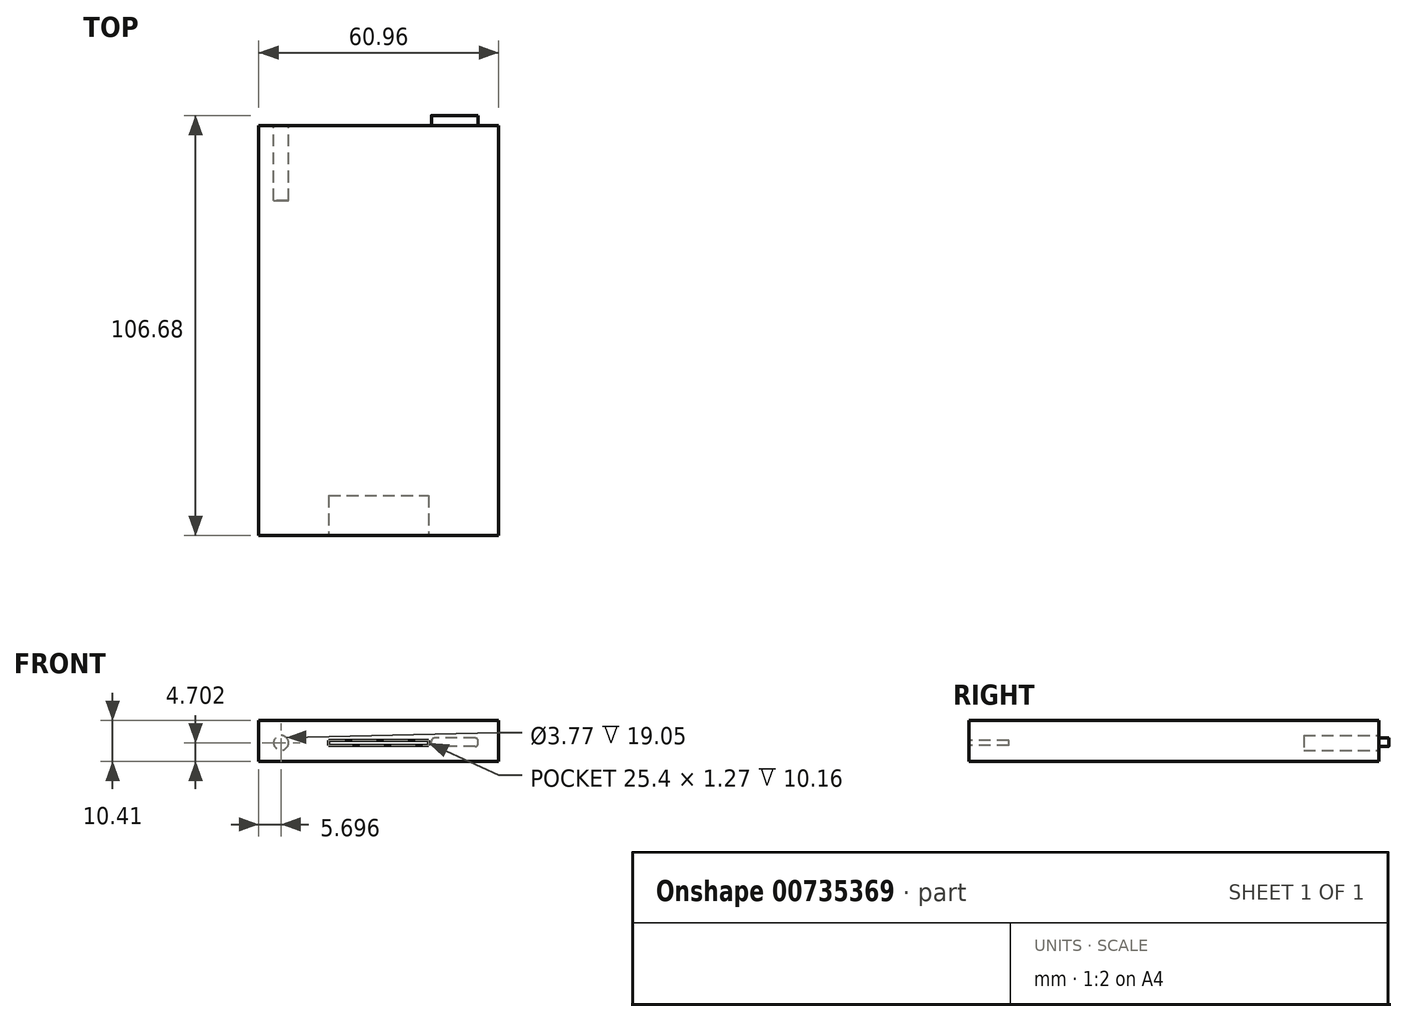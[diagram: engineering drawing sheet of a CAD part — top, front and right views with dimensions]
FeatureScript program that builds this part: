
annotation { "Feature Type Name" : "Feature", "Feature Type Description" : "" }
export const myFeature = defineFeature(function(context is Context, id is Id, definition is map)
    precondition{}
    {
        {
            var Q0;
            Q0=qCreatedBy(makeId("Top.planeOp"),FACE);
            var sketch = newSketch(context, id + "F0", { "sketchPlane" : qUnion([Q0])});
            skLineSegment(sketch, "E0.bottom", {"start": v(30.48, 52.07) * mm, "end": v(-30.48, 52.07) * mm});
            skLineSegment(sketch, "E0.top", {"start": v(30.48, -52.07) * mm, "end": v(-30.48, -52.07) * mm});
            skLineSegment(sketch, "E0.left", {"start": v(30.48, 52.07) * mm, "end": v(30.48, -52.07) * mm});
            skLineSegment(sketch, "E0.right", {"start": v(-30.48, 52.07) * mm, "end": v(-30.48, -52.07) * mm});
            skPoint(sketch, "E0.middle", {"position": v(0, 0) * mm});
            skLineSegment(sketch, "E1.bottom", {"start": v(-25.2, 47.14) * mm, "end": v(24.52, 47.14) * mm});
            skLineSegment(sketch, "E1.top", {"start": v(-25.2, 10.65) * mm, "end": v(24.52, 10.65) * mm});
            skLineSegment(sketch, "E1.left", {"start": v(-25.2, 47.14) * mm, "end": v(-25.2, 10.65) * mm});
            skLineSegment(sketch, "E1.right", {"start": v(24.52, 47.14) * mm, "end": v(24.52, 10.65) * mm});
            skSolve(sketch);
        }
        {
            var Q0;
            Q0=makeQuery(id+"F0.imprint","IMPRINT",FACE,{"disambiguationData":[TD([[makeQuery(id+"F0.imprint","IMPRINT",EDGE,{"derivedFrom":sQuery(id+"F0.wireOp",EDGE,"E1.bottom")}),-1.0]])]});
            var Q1;
            Q1=makeQuery(id+"F0.imprint","IMPRINT",FACE,{"disambiguationData":[TD([[makeQuery(id+"F0.imprint","IMPRINT",EDGE,{"derivedFrom":sQuery(id+"F0.wireOp",EDGE,"E0.bottom")}),1.0]])]});
            extrude(context, id + "F1", {"entities" : qUnion([Q0, Q1]), "depth" : 10.4 * mm, "offsetDistance" : 25.4 * mm});
        }
        {
            var Q0;
            Q0=makeQuery(id+"F1.opExtrude","SWEPT_FACE",FACE,{"disambiguationData":[OSD([sQuery(id+"F0.wireOp",EDGE,"E0.top")])]});
            var sketch = newSketch(context, id + "F2", { "sketchPlane" : qUnion([Q0])});
            skLineSegment(sketch, "E2.bottom", {"start": v(-12.7, 4.11) * mm, "end": v(12.7, 4.11) * mm});
            skLineSegment(sketch, "E2.top", {"start": v(-12.7, 5.38) * mm, "end": v(12.7, 5.38) * mm});
            skLineSegment(sketch, "E2.left", {"start": v(-12.7, 4.11) * mm, "end": v(-12.7, 5.38) * mm});
            skLineSegment(sketch, "E2.right", {"start": v(12.7, 4.11) * mm, "end": v(12.7, 5.38) * mm});
            skSolve(sketch);
        }
        {
            var Q0;
            Q0=makeQuery(id+"F2.imprint","IMPRINT",FACE,{"disambiguationData":[TD([[makeQuery(id+"F2.imprint","IMPRINT",EDGE,{"derivedFrom":sQuery(id+"F2.wireOp",EDGE,"E2.bottom")}),1.0]])]});
            extrude(context, id + "F3", {"entities" : qUnion([Q0]), "operationType" : NewBodyOperationType.REMOVE, "oppositeDirection" : true, "depth" : 10.16 * mm, "offsetDistance" : 25.4 * mm});
        }
        {
            var Q0;
            Q0=makeQuery(id+"F1.opExtrude","SWEPT_FACE",FACE,{"disambiguationData":[OSD([sQuery(id+"F0.wireOp",EDGE,"E0.bottom")])]});
            var sketch = newSketch(context, id + "F4", { "sketchPlane" : qUnion([Q0])});
            skCircle(sketch, "E3", {"center": v(24.78, 4.7) * mm, "radius": 1.88 * mm});
            skSolve(sketch);
        }
        {
            var Q0;
            Q0=makeQuery(id+"F4.imprint","IMPRINT",FACE,{"disambiguationData":[TD([[makeQuery(id+"F4.imprint","IMPRINT",EDGE,{"derivedFrom":sQuery(id+"F4.wireOp",EDGE,"E3")}),1.0]])]});
            extrude(context, id + "F5", {"entities" : qUnion([Q0]), "operationType" : NewBodyOperationType.REMOVE, "oppositeDirection" : true, "depth" : 19.05 * mm, "offsetDistance" : 25.4 * mm});
        }
        {
            var Q0;
            Q0=makeQuery(id+"F1.opExtrude","SWEPT_FACE",FACE,{"disambiguationData":[OSD([sQuery(id+"F0.wireOp",EDGE,"E0.bottom")])]});
            var sketch = newSketch(context, id + "F6", { "sketchPlane" : qUnion([Q0])});
            skLineSegment(sketch, "E4.bottom", {"start": v(-25.3, 3.8) * mm, "end": v(-13.42, 3.8) * mm});
            skLineSegment(sketch, "E4.top", {"start": v(-25.3, 5.9) * mm, "end": v(-13.42, 5.9) * mm});
            skLineSegment(sketch, "E4.left", {"start": v(-25.3, 3.8) * mm, "end": v(-25.3, 5.9) * mm});
            skLineSegment(sketch, "E4.right", {"start": v(-13.42, 3.8) * mm, "end": v(-13.42, 5.9) * mm});
            skSolve(sketch);
        }
        {
            var Q0;
            Q0=makeQuery(id+"F6.imprint","IMPRINT",FACE,{"disambiguationData":[TD([[makeQuery(id+"F6.imprint","IMPRINT",EDGE,{"derivedFrom":sQuery(id+"F6.wireOp",EDGE,"E4.bottom")}),1.0]])]});
            extrude(context, id + "F7", {"entities" : qUnion([Q0]), "operationType" : NewBodyOperationType.ADD, "depth" : 2.54 * mm, "offsetDistance" : 25.4 * mm});
        }
        {
            var Q0;
            Q0=makeQuery(id+"F7.opExtrude","SWEPT_EDGE",EDGE,{"disambiguationData":[OSD([sQuery(id+"F6.wireOp",EDGE,"E4.bottom"),sQuery(id+"F6.wireOp",EDGE,"E4.right")])]});
            var Q1;
            Q1=makeQuery(id+"F7.opExtrude","SWEPT_EDGE",EDGE,{"disambiguationData":[OSD([sQuery(id+"F6.wireOp",EDGE,"E4.bottom"),sQuery(id+"F6.wireOp",EDGE,"E4.left")])]});
            var Q2;
            Q2=makeQuery(id+"F7.opExtrude","SWEPT_EDGE",EDGE,{"disambiguationData":[OSD([sQuery(id+"F6.wireOp",EDGE,"E4.top"),sQuery(id+"F6.wireOp",EDGE,"E4.left")])]});
            var Q3;
            Q3=makeQuery(id+"F7.opExtrude","SWEPT_EDGE",EDGE,{"disambiguationData":[OSD([sQuery(id+"F6.wireOp",EDGE,"E4.top"),sQuery(id+"F6.wireOp",EDGE,"E4.right")])]});
            fillet(context, id + "F8", {"entities" : qUnion([Q0, Q1, Q2, Q3]), "radius" : 0.76 * mm, "tangentPropagation" : true, "allowEdgeOverflow" : false});
        }
    });
